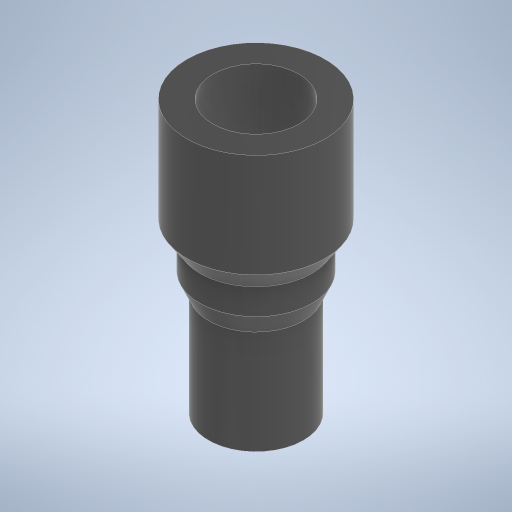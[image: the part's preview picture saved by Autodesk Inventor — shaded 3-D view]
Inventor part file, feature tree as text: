
AUTODESK INVENTOR PART (.ipt)
format: ipt  version: 2024 (Build 280153000, 153)  size: 269,312 bytes
history: native  units: mm
features: extrude x5, sketch x5, other x4, plane x2, loft x2
ambient origin geometry x8: Origin, YZ Plane, XZ Plane, XY Plane, X Axis, Y Axis, Z Axis, Center Point
bodies: Solid1 (feature_tree)
feature tree (18):
  extrude  "Extrusion1"  Depth=12.0mm TaperAngle=0.0deg
  extrude  "Extrusion2"  Depth=10.0mm TaperAngle=0.0deg
  plane  "Work Plane1"
  extrude  "Extrusion3"  Depth=13.0mm
  loft  "Loft1"
  plane  "Work Plane2"
  extrude  "Extrusion4"  Depth=10.0mm
  loft  "Loft2"
  extrude  "Extrusion5"  Depth=10.0mm TaperAngle=0.0deg
  sketch  "Sketch1"  dims[d0=11.0mm d1=12.0mm d2=0.0mm]
  sketch  "Sketch2"  dims[d3=6.0mm d4=10.0mm d5=0.0mm]
  sketch  "Sketch3"  dims[d6=2.25mm d7=13.0mm]
  other  "Edges1"
  other  "Edges2"
  sketch  "Sketch4"  dims[d8=3.0mm d9=0.0mm d10=0.0mm d11=90.0deg]
  other  "Edges3"
  other  "Edges4"
  sketch  "Sketch5"  dims[d12=0.0mm d13=90.0deg d14=2.25mm d15=16.0mm d16=12.0mm d17=0.0mm d18=0.0mm d19=90.0deg d20=0.0mm d21=90.0deg d22=10.0mm d23=10.0mm d24=0.0mm]
